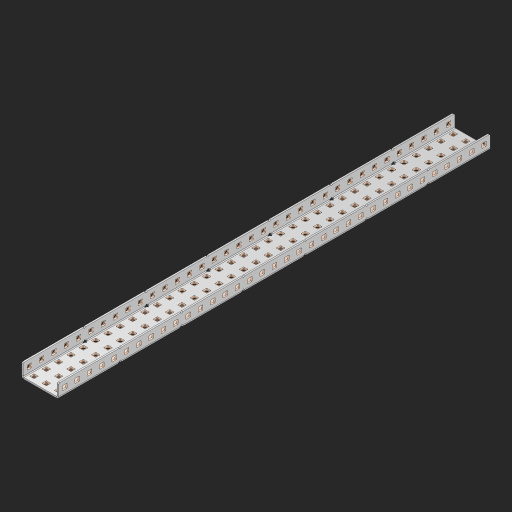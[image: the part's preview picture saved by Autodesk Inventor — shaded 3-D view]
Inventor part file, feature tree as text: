
AUTODESK INVENTOR PART (.ipt)
format: ipt  version: 2023 (Build 270158000, 158)  size: 2,031,616 bytes
history: native  units: in
note: dims shown in document units (in); Inventor stores cm internally (conversion verified against a paired STEP export)
features: other x180, extrude x174, sheet_metal_op x10, sketch x8, mirror x1, pattern_linear x1, chamfer x1
ambient origin geometry x8: Origin, YZ Plane, XZ Plane, XY Plane, X Axis, Y Axis, Z Axis, Center Point
bodies: Solid1 (feature_tree), Body (feature_tree)
feature tree (375):
  other  "Flange Pattern Plane"
  sheet_metal_op  "Flange Pattern"
  sheet_metal_op  "Body Pattern"
  other  "Arc Length"
  mirror  "Notch Mirror"
  pattern_linear  "Notch Pattern"  Spacing1=0.25in  [1 undecoded]
  chamfer  "End Chamfer"
  extrude  "Half Cut"  Depth=0.0625in
  sketch  "Sketch1"  dims[d0=1.5in]
  other  "Plate1"
  sketch  "Sketch2"  dims[d1=17.5in]
  other  "Plate2"
  sheet_metal_op  "Bend1"
  sheet_metal_op  "Corner1"
  sketch  "Sketch3"  dims[d2=0.0625in]
  other  "Flange Pattern Sketch"
  sketch  "Sketch7"  dims[d3=0.0625in]
  other  "Srf1"
  other  "Srf2"
  sketch  "Sketch8"  dims[d4=0.0312in]
  sketch  "Sketch9"  dims[d5=0.125in]
  other  "Srf91"
  sheet_metal_op  "Body Pattern Sketch"
  other  "Srf92"
  sketch  "Sketch13"  dims[d6=0.0625in]
  sketch  "Sketch14"  dims[d7=0.5in d8=90.0deg d9=0.0312in d10=0.25in d11=0.0625in d12=0.0625in d16=0.182in d17=0.02in d18=0.0625in d19=0.0in d20=0.25in d21=0.25in d46=0.172in d47=1.0in d48=0.0in d49=0.182in d50=0.02in d51=0.25in d52=0.25in d53=0.0625in d54=0.0in d55=0.172in d56=1.0in d57=0.0in d60=13.7795in d62=0.5in d63=1.1811in d65=0.5in d85=0.1473in d86=0.1782in d88=0.04in d89=0.0625in d90=0.0in d91=0.04in d92=0.0491in d95=2.5in d96=0.04in d97=0.25in d98=45.0deg d101=0.0in d102=2.497in d131=1.5in d132=13.7795in d134=0.5in d139=0.5in]
  other  "Srf856"
  other  "Srf1310"
  other  "Srf1311"
  other  "Srf1312"
  other  "Srf1376"
  other  "Srf1377"
  other  "Srf1728"
  other  "Srf1755"
  other  "Srf1878"
  other  "Srf1879"
  other  "Srf1880"
  other  "Srf1881"
  other  "Srf1882"
  other  "Srf1883"
  other  "Srf1884"
  other  "Srf1885"
  other  "Srf1886"
  other  "Srf1887"
  other  "Srf1888"
  other  "Srf1889"
  other  "Srf1890"
  other  "Srf1891"
  other  "Srf1892"
  other  "Srf1893"
  other  "Srf1894"
  other  "Srf1895"
  other  "Srf1896"
  other  "Srf1897"
  other  "Srf1898"
  other  "Srf1899"
  other  "Srf1900"
  other  "Srf1901"
  other  "Srf1902"
  other  "Srf1903"
  other  "Srf1904"
  other  "Srf1905"
  other  "Srf1906"
  other  "Srf1907"
  other  "Srf1908"
  other  "Srf1909"
  other  "Srf1910"
  other  "Srf1911"
  other  "Srf1912"
  other  "Srf1913"
  other  "Srf1914"
  other  "Srf1915"
  other  "Srf1916"
  other  "Srf1917"
  other  "Srf1918"
  other  "Srf1919"
  other  "Srf1920"
  other  "Srf1921"
  other  "Srf1922"
  other  "Srf1923"
  other  "Srf1924"
  other  "Srf1925"
  other  "Srf1926"
  other  "Srf1927"
  other  "Srf1928"
  other  "Srf1929"
  other  "Srf1930"
  other  "Srf1931"
  other  "Srf1932"
  other  "Srf1933"
  other  "Srf1934"
  other  "Srf1935"
  other  "Srf1936"
  other  "Srf1937"
  other  "Srf1938"
  other  "Srf1939"
  other  "Srf1940"
  other  "Srf1941"
  other  "Srf1942"
  other  "Srf1943"
  other  "Srf1944"
  other  "Srf1945"
  other  "Srf1946"
  other  "Srf1947"
  other  "Srf1948"
  other  "Srf1949"
  other  "Srf1950"
  other  "Srf1951"
  other  "Srf1952"
  other  "Srf1953"
  other  "Srf1954"
  other  "Srf1955"
  other  "Srf1956"
  other  "Srf1957"
  other  "Srf1958"
  other  "Srf1959"
  other  "Srf1960"
  other  "Srf1961"
  other  "Srf1962"
  other  "Srf1963"
  other  "Srf1964"
  other  "Srf1965"
  other  "Srf1966"
  other  "Srf1967"
  other  "Srf1968"
  other  "Srf1969"
  other  "Srf1970"
  other  "Srf1971"
  other  "Srf1972"
  other  "Srf1973"
  other  "Srf1974"
  other  "Srf1975"
  other  "Srf1976"
  other  "Srf1977"
  other  "Srf1978"
  other  "Srf1979"
  other  "Srf1980"
  other  "Srf1981"
  other  "Srf1982"
  other  "Srf1983"
  other  "Srf1984"
  other  "Srf1985"
  other  "Srf1986"
  other  "Srf1987"
  other  "Srf1988"
  other  "Srf1989"
  other  "Srf1990"
  other  "Srf1991"
  other  "Srf1992"
  other  "Srf1993"
  other  "Srf1994"
  other  "Srf1995"
  other  "Srf1996"
  other  "Srf1997"
  other  "Srf1998"
  other  "Srf1999"
  other  "Srf2000"
  other  "Srf2001"
  other  "Srf2002"
  other  "Srf2003"
  other  "Srf2004"
  other  "Srf2005"
  other  "Srf2006"
  other  "Srf2007"
  other  "Srf2008"
  other  "Srf2009"
  other  "Srf2010"
  other  "Srf2011"
  other  "Srf2012"
  other  "Srf2013"
  other  "Srf2014"
  other  "Srf2015"
  other  "Srf2016"
  other  "Srf2017"
  other  "Srf2018"
  other  "Srf2019"
  other  "Srf2020"
  other  "Srf2021"
  other  "Srf2022"
  other  "Srf2023"
  other  "Srf2024"
  other  "Srf2025"
  other  "Srf2026"
  other  "Srf2027"
  other  "Srf2028"
  other  "Srf2029"
  other  "Srf2030"
  other  "Srf2031"
  other  "Srf2032"
  other  "Srf2033"
  other  "Srf2034"
  other  "Srf2035"
  other  "Srf2036"
  other  "Srf2037"
  other  "Srf2038"
  other  "Srf2039"
  other  "Srf2040"
  sheet_metal_op  "Flange Stamp"
  sheet_metal_op  "Flange Circle"
  sheet_metal_op  "Body Stamp"
  sheet_metal_op  "Body Circle"
  sheet_metal_op  "Notch"
  extrude  "ExtrusionSrf2"  Depth=0.0625in
  extrude  "ExtrusionSrf92"  Depth=1.5in
  extrude  "ExtrusionSrf856"  Depth=0.02in
  extrude  "ExtrusionSrf1310"  Depth=0.0625in
  extrude  "ExtrusionSrf1311"  TaperAngle=0.0deg  [1 undecoded]
  extrude  "ExtrusionSrf1312"  Depth=0.25in
  extrude  "ExtrusionSrf1376"  Depth=0.25in
  extrude  "ExtrusionSrf1377"  Depth=1.5in
  extrude  "ExtrusionSrf1728"  Depth=1.5in TaperAngle=0.0deg
  extrude  "ExtrusionSrf1755"  Depth=1.5in
  extrude  "ExtrusionSrf1878"  Depth=0.02in
  extrude  "ExtrusionSrf1879"  Depth=0.25in
  extrude  "ExtrusionSrf1880"  Depth=0.25in
  extrude  "ExtrusionSrf1881"  Depth=0.0625in
  extrude  "ExtrusionSrf1882"  TaperAngle=0.0deg  [1 undecoded]
  extrude  "ExtrusionSrf1883"  Depth=1.5in
  extrude  "ExtrusionSrf1884"  Depth=1.5in TaperAngle=0.0deg
  extrude  "ExtrusionSrf1885"  Depth=1.5in
  extrude  "ExtrusionSrf1886"  Depth=1.5in
  extrude  "ExtrusionSrf1887"  Depth=1.5in
  extrude  "ExtrusionSrf1888"  Depth=1.5in
  extrude  "ExtrusionSrf1889"  Depth=1.5in
  extrude  "ExtrusionSrf1890"  Depth=0.0625in
  extrude  "ExtrusionSrf1891"  TaperAngle=0.0deg  [1 undecoded]
  extrude  "ExtrusionSrf1892"  Depth=1.5in
  extrude  "ExtrusionSrf1893"  Depth=1.5in
  extrude  "ExtrusionSrf1894"  Depth=1.5in
  extrude  "ExtrusionSrf1895"  Depth=0.25in TaperAngle=45.0deg
  extrude  "ExtrusionSrf1896"  TaperAngle=0.0deg  [1 undecoded]
  extrude  "ExtrusionSrf1897"  Depth=1.5in
  extrude  "ExtrusionSrf1898"  Depth=1.5in
  extrude  "ExtrusionSrf1899"  Depth=1.5in
  extrude  "ExtrusionSrf1900"  Depth=1.5in
  extrude  "ExtrusionSrf1901"  Depth=1.5in
  extrude  "ExtrusionSrf1902"  [1 undecoded]
  extrude  "ExtrusionSrf1903"  [1 undecoded]
  extrude  "ExtrusionSrf1904"  [1 undecoded]
  extrude  "ExtrusionSrf1905"  [1 undecoded]
  extrude  "ExtrusionSrf1906"  [1 undecoded]
  extrude  "ExtrusionSrf1907"  [1 undecoded]
  extrude  "ExtrusionSrf1908"  [1 undecoded]
  extrude  "ExtrusionSrf1909"  [1 undecoded]
  extrude  "ExtrusionSrf1910"  [1 undecoded]
  extrude  "ExtrusionSrf1911"  [1 undecoded]
  extrude  "ExtrusionSrf1912"  [1 undecoded]
  extrude  "ExtrusionSrf1913"  [1 undecoded]
  extrude  "ExtrusionSrf1914"  [1 undecoded]
  extrude  "ExtrusionSrf1915"  [1 undecoded]
  extrude  "ExtrusionSrf1916"  [1 undecoded]
  extrude  "ExtrusionSrf1917"  [1 undecoded]
  extrude  "ExtrusionSrf1918"  [1 undecoded]
  extrude  "ExtrusionSrf1919"  [1 undecoded]
  extrude  "ExtrusionSrf1920"  [1 undecoded]
  extrude  "ExtrusionSrf1921"  [1 undecoded]
  extrude  "ExtrusionSrf1922"  [1 undecoded]
  extrude  "ExtrusionSrf1923"  [1 undecoded]
  extrude  "ExtrusionSrf1924"  [1 undecoded]
  extrude  "ExtrusionSrf1925"  [1 undecoded]
  extrude  "ExtrusionSrf1926"  [1 undecoded]
  extrude  "ExtrusionSrf1927"  [1 undecoded]
  extrude  "ExtrusionSrf1928"  [1 undecoded]
  extrude  "ExtrusionSrf1929"  [1 undecoded]
  extrude  "ExtrusionSrf1930"  [1 undecoded]
  extrude  "ExtrusionSrf1931"  [1 undecoded]
  extrude  "ExtrusionSrf1932"  [1 undecoded]
  extrude  "ExtrusionSrf1933"  [1 undecoded]
  extrude  "ExtrusionSrf1934"  [1 undecoded]
  extrude  "ExtrusionSrf1935"  [1 undecoded]
  extrude  "ExtrusionSrf1936"  [1 undecoded]
  extrude  "ExtrusionSrf1937"  [1 undecoded]
  extrude  "ExtrusionSrf1938"  [1 undecoded]
  extrude  "ExtrusionSrf1939"  [1 undecoded]
  extrude  "ExtrusionSrf1940"  [1 undecoded]
  extrude  "ExtrusionSrf1941"  [1 undecoded]
  extrude  "ExtrusionSrf1942"  [1 undecoded]
  extrude  "ExtrusionSrf1943"  [1 undecoded]
  extrude  "ExtrusionSrf1944"  [1 undecoded]
  extrude  "ExtrusionSrf1945"  [1 undecoded]
  extrude  "ExtrusionSrf1946"  [1 undecoded]
  extrude  "ExtrusionSrf1947"  [1 undecoded]
  extrude  "ExtrusionSrf1948"  [1 undecoded]
  extrude  "ExtrusionSrf1949"  [1 undecoded]
  extrude  "ExtrusionSrf1950"  [1 undecoded]
  extrude  "ExtrusionSrf1951"  [1 undecoded]
  extrude  "ExtrusionSrf1952"  [1 undecoded]
  extrude  "ExtrusionSrf1953"  [1 undecoded]
  extrude  "ExtrusionSrf1954"  [1 undecoded]
  extrude  "ExtrusionSrf1955"  [1 undecoded]
  extrude  "ExtrusionSrf1956"  [1 undecoded]
  extrude  "ExtrusionSrf1957"  [1 undecoded]
  extrude  "ExtrusionSrf1958"  [1 undecoded]
  extrude  "ExtrusionSrf1959"  [1 undecoded]
  extrude  "ExtrusionSrf1960"  [1 undecoded]
  extrude  "ExtrusionSrf1961"  [1 undecoded]
  extrude  "ExtrusionSrf1962"  [1 undecoded]
  extrude  "ExtrusionSrf1963"  [1 undecoded]
  extrude  "ExtrusionSrf1964"  [1 undecoded]
  extrude  "ExtrusionSrf1965"  [1 undecoded]
  extrude  "ExtrusionSrf1966"  [1 undecoded]
  extrude  "ExtrusionSrf1967"  [1 undecoded]
  extrude  "ExtrusionSrf1968"  [1 undecoded]
  extrude  "ExtrusionSrf1969"  [1 undecoded]
  extrude  "ExtrusionSrf1970"  [1 undecoded]
  extrude  "ExtrusionSrf1971"  [1 undecoded]
  extrude  "ExtrusionSrf1972"  [1 undecoded]
  extrude  "ExtrusionSrf1973"  [1 undecoded]
  extrude  "ExtrusionSrf1974"  [1 undecoded]
  extrude  "ExtrusionSrf1975"  [1 undecoded]
  extrude  "ExtrusionSrf1976"  [1 undecoded]
  extrude  "ExtrusionSrf1977"  [1 undecoded]
  extrude  "ExtrusionSrf1978"  [1 undecoded]
  extrude  "ExtrusionSrf1979"  [1 undecoded]
  extrude  "ExtrusionSrf1980"  [1 undecoded]
  extrude  "ExtrusionSrf1981"  [1 undecoded]
  extrude  "ExtrusionSrf1982"  [1 undecoded]
  extrude  "ExtrusionSrf1983"  [1 undecoded]
  extrude  "ExtrusionSrf1984"  [1 undecoded]
  extrude  "ExtrusionSrf1985"  [1 undecoded]
  extrude  "ExtrusionSrf1986"  [1 undecoded]
  extrude  "ExtrusionSrf1987"  [1 undecoded]
  extrude  "ExtrusionSrf1988"  [1 undecoded]
  extrude  "ExtrusionSrf1989"  [1 undecoded]
  extrude  "ExtrusionSrf1990"  [1 undecoded]
  extrude  "ExtrusionSrf1991"  [1 undecoded]
  extrude  "ExtrusionSrf1992"  [1 undecoded]
  extrude  "ExtrusionSrf1993"  [1 undecoded]
  extrude  "ExtrusionSrf1994"  [1 undecoded]
  extrude  "ExtrusionSrf1995"  [1 undecoded]
  extrude  "ExtrusionSrf1996"  [1 undecoded]
  extrude  "ExtrusionSrf1997"  [1 undecoded]
  extrude  "ExtrusionSrf1998"  [1 undecoded]
  extrude  "ExtrusionSrf1999"  [1 undecoded]
  extrude  "ExtrusionSrf2000"  [1 undecoded]
  extrude  "ExtrusionSrf2001"  [1 undecoded]
  extrude  "ExtrusionSrf2002"  [1 undecoded]
  extrude  "ExtrusionSrf2003"  [1 undecoded]
  extrude  "ExtrusionSrf2004"  [1 undecoded]
  extrude  "ExtrusionSrf2005"  [1 undecoded]
  extrude  "ExtrusionSrf2006"  [1 undecoded]
  extrude  "ExtrusionSrf2007"  [1 undecoded]
  extrude  "ExtrusionSrf2008"  [1 undecoded]
  extrude  "ExtrusionSrf2009"  [1 undecoded]
  extrude  "ExtrusionSrf2010"  [1 undecoded]
  extrude  "ExtrusionSrf2011"  [1 undecoded]
  extrude  "ExtrusionSrf2012"  [1 undecoded]
  extrude  "ExtrusionSrf2013"  [1 undecoded]
  extrude  "ExtrusionSrf2014"  [1 undecoded]
  extrude  "ExtrusionSrf2015"  [1 undecoded]
  extrude  "ExtrusionSrf2016"  [1 undecoded]
  extrude  "ExtrusionSrf2017"  [1 undecoded]
  extrude  "ExtrusionSrf2018"  [1 undecoded]
  extrude  "ExtrusionSrf2019"  [1 undecoded]
  extrude  "ExtrusionSrf2020"  [1 undecoded]
  extrude  "ExtrusionSrf2021"  [1 undecoded]
  extrude  "ExtrusionSrf2022"  [1 undecoded]
  extrude  "ExtrusionSrf2023"  [1 undecoded]
  extrude  "ExtrusionSrf2024"  [1 undecoded]
  extrude  "ExtrusionSrf2025"  [1 undecoded]
  extrude  "ExtrusionSrf2026"  [1 undecoded]
  extrude  "ExtrusionSrf2027"  [1 undecoded]
  extrude  "ExtrusionSrf2028"  [1 undecoded]
  extrude  "ExtrusionSrf2029"  [1 undecoded]
  extrude  "ExtrusionSrf2030"  [1 undecoded]
  extrude  "ExtrusionSrf2031"  [1 undecoded]
  extrude  "ExtrusionSrf2032"  [1 undecoded]
  extrude  "ExtrusionSrf2033"  [1 undecoded]
  extrude  "ExtrusionSrf2034"  [1 undecoded]
  extrude  "ExtrusionSrf2035"  [1 undecoded]
  extrude  "ExtrusionSrf2036"  [1 undecoded]
  extrude  "ExtrusionSrf2037"  [1 undecoded]
  extrude  "ExtrusionSrf2038"  [1 undecoded]
  extrude  "ExtrusionSrf2039"  [1 undecoded]
  extrude  "ExtrusionSrf2040"  [1 undecoded]
note: 144 required parameter values undecoded (feature->parameter linkage not recoverable at this tier; creation-order binding heuristic only, values carry confidence <= 0.55)
